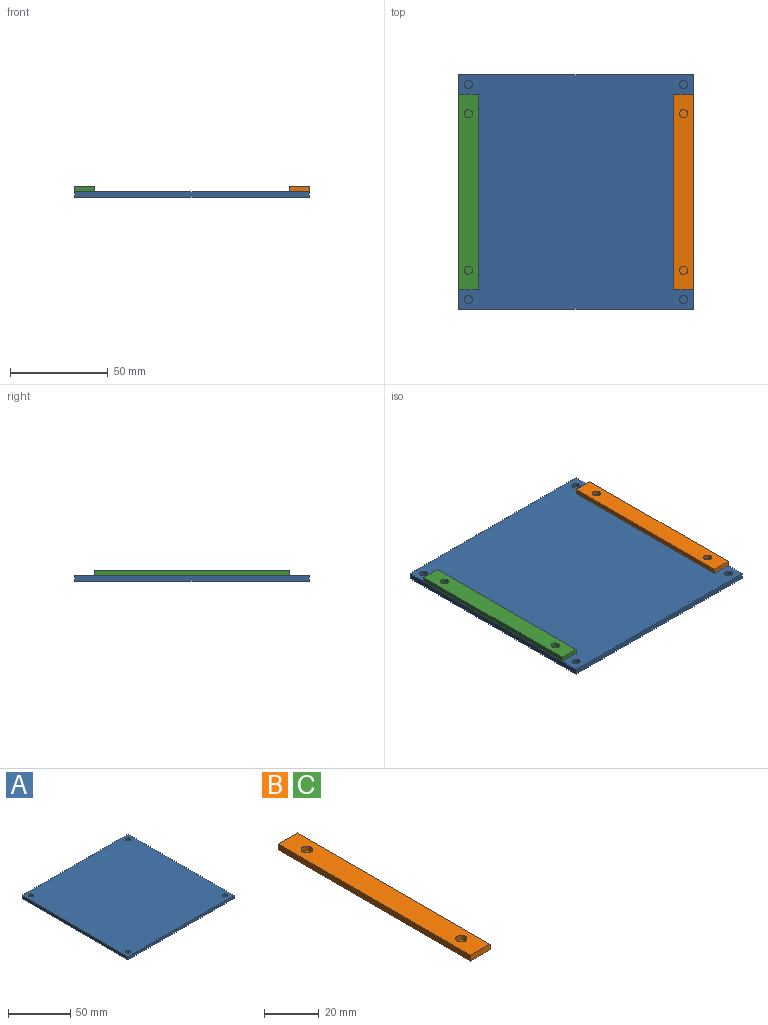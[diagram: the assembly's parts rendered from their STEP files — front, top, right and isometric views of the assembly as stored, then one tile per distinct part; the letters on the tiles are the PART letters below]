
ASSEMBLY  parts=3 mates=2
PART A: 14 faces, bbox 120x120x3 mm
  f0: plane 120x3mm, normal (0,1,0), area 360mm2, adj f1,f3,f4,f5
  f1: plane 120x3mm, normal (-1,0,0), area 360mm2, adj f0,f2,f4,f5
  f2: plane 120x3mm, normal (0,-1,0), area 360mm2, adj f1,f3,f4,f5
  f3: plane 120x3mm, normal (1,0,0), area 360mm2, adj f0,f2,f4,f5
  f4: plane 120x120mm, normal (0,0,1), area 14344.6mm2, adj f0,f1,f2,f3,f6,f8,f10,f12
  f5: plane 120x120mm, normal (0,0,-1), area 14400mm2, adj f0,f1,f2,f3
  f6: cylinder r=2.1mm len=4.2mm, axis (0,0,1), area 26.4mm2, adj f4,f7
  f7: plane 4.2x4.2mm, normal (0,0,1), area 13.9mm2, adj f6
  f8: cylinder r=2.1mm len=4.2mm, axis (0,0,1), area 26.4mm2, adj f4,f9
  f9: plane 4.2x4.2mm, normal (0,0,1), area 13.9mm2, adj f8
  f10: cylinder r=2.1mm len=4.2mm, axis (0,0,1), area 26.4mm2, adj f4,f11
  f11: plane 4.2x4.2mm, normal (0,0,1), area 13.9mm2, adj f10
  f12: cylinder r=2.1mm len=4.2mm, axis (0,0,1), area 26.4mm2, adj f4,f13
  f13: plane 4.2x4.2mm, normal (0,0,1), area 13.9mm2, adj f12
PART B: 10 faces, bbox 10x100x2.6 mm
  f0: plane 10x2.6mm, normal (0,1,0), area 26mm2, adj f1,f3,f4,f5
  f1: plane 100x2.6mm, normal (-1,0,0), area 260mm2, adj f0,f2,f4,f5
  f2: plane 10x2.6mm, normal (0,-1,0), area 26mm2, adj f1,f3,f4,f5
  f3: plane 100x2.6mm, normal (1,0,0), area 260mm2, adj f0,f2,f4,f5
  f4: plane 100x10mm, normal (0,0,1), area 972.3mm2, adj f0,f1,f2,f3,f6,f8
  f5: plane 100x10mm, normal (0,0,-1), area 1000mm2, adj f0,f1,f2,f3
  f6: cylinder r=2.1mm len=4.2mm, axis (0,0,1), area 26.4mm2, adj f4,f7
  f7: plane 4.2x4.2mm, normal (0,0,1), area 13.9mm2, adj f6
  f8: cylinder r=2.1mm len=4.2mm, axis (0,0,1), area 26.4mm2, adj f4,f9
  f9: plane 4.2x4.2mm, normal (0,0,1), area 13.9mm2, adj f8
PART C: same geometry as B
PLACE A t=(-0.16,0.08,0.25)mm
PLACE B t=(54.84,0.08,1.75)mm
PLACE C t=(-55.16,0.08,1.75)mm
MATE fastened B.f5 <-> A.f4  axis (0,0,-1) through (59.84,0.08,1.75)mm
MATE fastened C.f5 <-> A.f4  axis (0,0,-1) through (-60.16,0.08,1.75)mm
